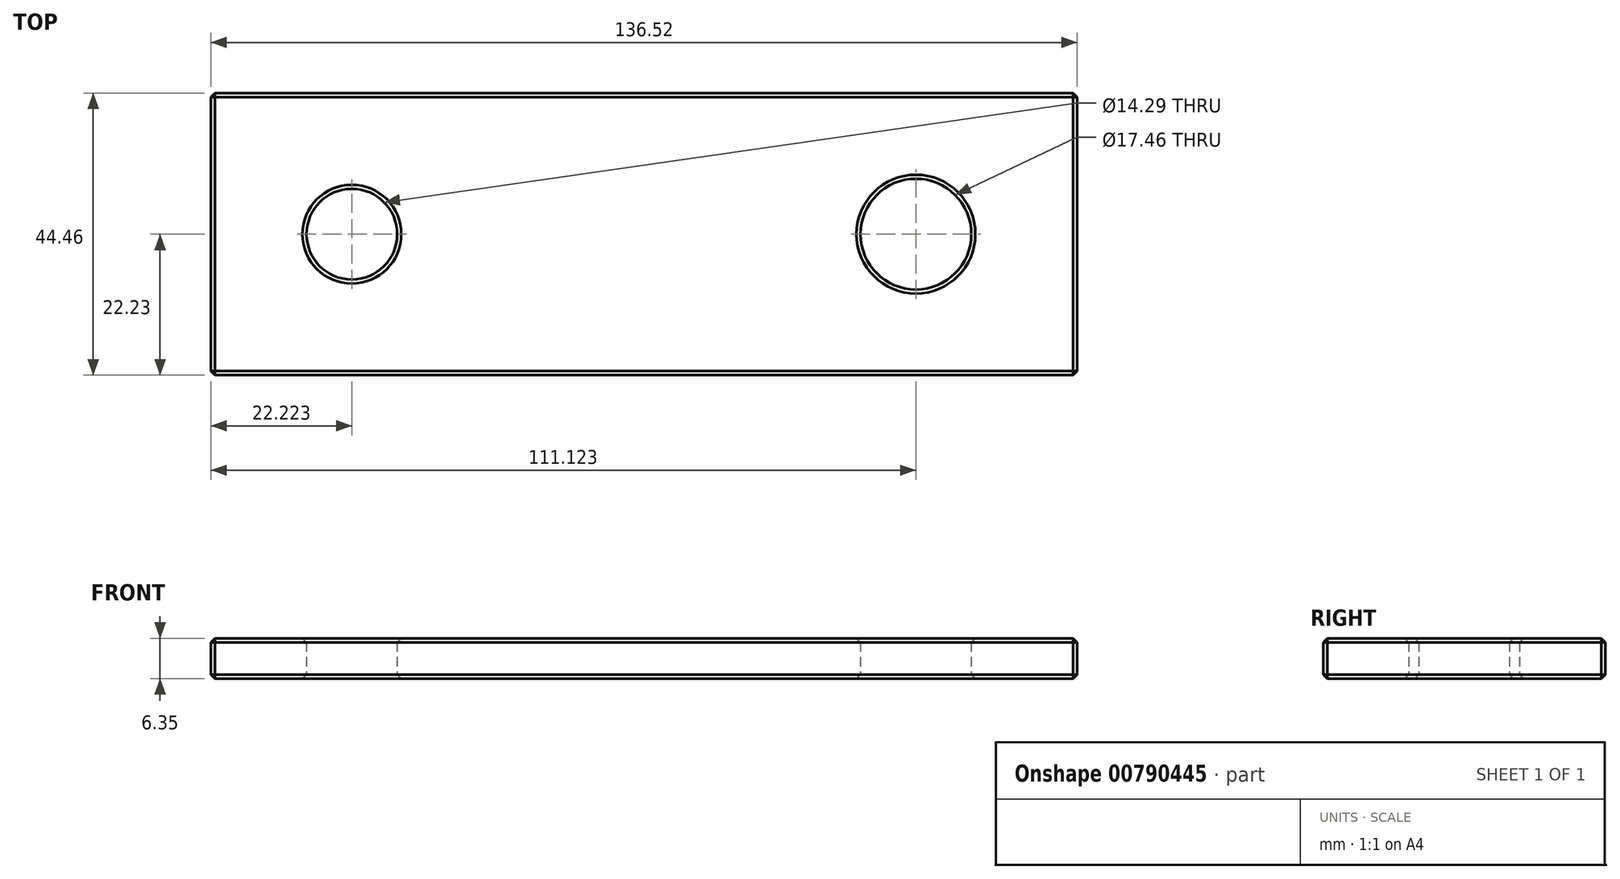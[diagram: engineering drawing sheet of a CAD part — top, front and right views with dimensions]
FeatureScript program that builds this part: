
annotation { "Feature Type Name" : "Feature", "Feature Type Description" : "" }
export const myFeature = defineFeature(function(context is Context, id is Id, definition is map)
    precondition{}
    {
        {
            var Q0;
            Q0=qCreatedBy(makeId("Top.planeOp"),FACE);
            var sketch = newSketch(context, id + "F0", { "sketchPlane" : qUnion([Q0])});
            skLineSegment(sketch, "E0.bottom", {"start": v(68.26, -22.22) * mm, "end": v(-68.26, -22.23) * mm});
            skLineSegment(sketch, "E0.top", {"start": v(68.26, 22.23) * mm, "end": v(-68.26, 22.22) * mm});
            skLineSegment(sketch, "E0.left", {"start": v(68.26, -22.22) * mm, "end": v(68.26, 22.23) * mm});
            skLineSegment(sketch, "E0.right", {"start": v(-68.26, -22.23) * mm, "end": v(-68.26, 22.22) * mm});
            skPoint(sketch, "E0.middle", {"position": v(0, 0) * mm});
            skCircle(sketch, "E1", {"center": v(-46.04, 0) * mm, "radius": 7.14 * mm});
            skCircle(sketch, "E2", {"center": v(42.86, 0) * mm, "radius": 8.73 * mm});
            skSolve(sketch);
        }
        {
            var Q0;
            Q0 = qSketchRegion(id + "F0", true);
            extrude(context, id + "F1", {"entities" : qUnion([Q0]), "depth" : 6.35 * mm, "offsetDistance" : 25.4 * mm});
        }
        {
            var Q0;
            Q0=makeQuery(id+"F1.opExtrude","SWEPT_FACE",FACE,{"disambiguationData":[OSD([sQuery(id+"F0.wireOp",EDGE,"E0.bottom")])]});
            var Q1;
            Q1=makeQuery(id+"F1.opExtrude","CAP_EDGE",EDGE,{"disambiguationData":[OSD([sQuery(id+"F0.wireOp",EDGE,"E0.left")])],"isStart":false});
            var Q2;
            Q2=makeQuery(id+"F1.opExtrude","CAP_EDGE",EDGE,{"disambiguationData":[OSD([sQuery(id+"F0.wireOp",EDGE,"E0.left")])],"isStart":true});
            var Q3;
            Q3=makeQuery(id+"F1.opExtrude","SWEPT_FACE",FACE,{"disambiguationData":[OSD([sQuery(id+"F0.wireOp",EDGE,"E0.top")])]});
            var Q4;
            Q4=makeQuery(id+"F1.opExtrude","CAP_EDGE",EDGE,{"disambiguationData":[OSD([sQuery(id+"F0.wireOp",EDGE,"E2")])],"isStart":false});
            var Q5;
            Q5=makeQuery(id+"F1.opExtrude","CAP_EDGE",EDGE,{"disambiguationData":[OSD([sQuery(id+"F0.wireOp",EDGE,"E1")])],"isStart":false});
            var Q6;
            Q6=makeQuery(id+"F1.opExtrude","SWEPT_FACE",FACE,{"disambiguationData":[OSD([sQuery(id+"F0.wireOp",EDGE,"E0.right")])]});
            var Q7;
            Q7=makeQuery(id+"F1.opExtrude","CAP_EDGE",EDGE,{"disambiguationData":[OSD([sQuery(id+"F0.wireOp",EDGE,"E1")])],"isStart":true});
            var Q8;
            Q8=makeQuery(id+"F1.opExtrude","CAP_EDGE",EDGE,{"disambiguationData":[OSD([sQuery(id+"F0.wireOp",EDGE,"E2")])],"isStart":true});
            chamfer(context, id + "F2", {"entities" : qUnion([Q0, Q1, Q2, Q3, Q4, Q5, Q6, Q7, Q8]), "width" : 0.64 * mm, "tangentPropagation" : true});
        }
    });
